# Revit family: Shower-Bath_Spout-KOHLER-Honesty-K-20004
name_source: partatom
category: Plumbing Fixtures
revit_build: Autodesk Revit 2015 (Build: 20140606_1530(x64)
units: mm (PartAtom-declared; Revit-internal decimal feet)

## types (1)
- CP-Polished Chrome
    ADA Compliant = No
    Assembly Code = D2010
    CW Connection = No
    Cold Water Inlet = Cold Water Inlet
    Date Modified = 06/22/2018
    Default Elevation = 36"
    Description = Wall-mount bath spout
    Drain Included = No
    Finish = Kohler-Metal-CP-Polished_Chrome
    Flow Rate = 0 GPM
    HW Connection = Yes
    Height = 1 13/16"
    Hot Water Inlet = Tempered Water Inlet
    Length = 7 3/8"
    Manufacturer = KOHLER Co.
    MasterFormat 1995 = 15410
    MasterFormat 2004 = 22.41.39
    Material = Premium Metal Construction
    Model = K-20004-CP
    Pressure = 0.00 psi
    Product Documentation Link = http://www.us.kohler.com
    Product Name = Honesty
    Product Page URL = http://www.us.kohler.com
    Spout Reach = 6 9/16"
    URL = https://www.us.kohler.com
    Vent Connection = No
    Waste Connection = No
    Waste Water Outlet = Waste Water Outlet
    Width = 1 7/8"

## geometry (parser evidence)
native form markers: Sweep x4
no freeform markers — native parametric forms only
